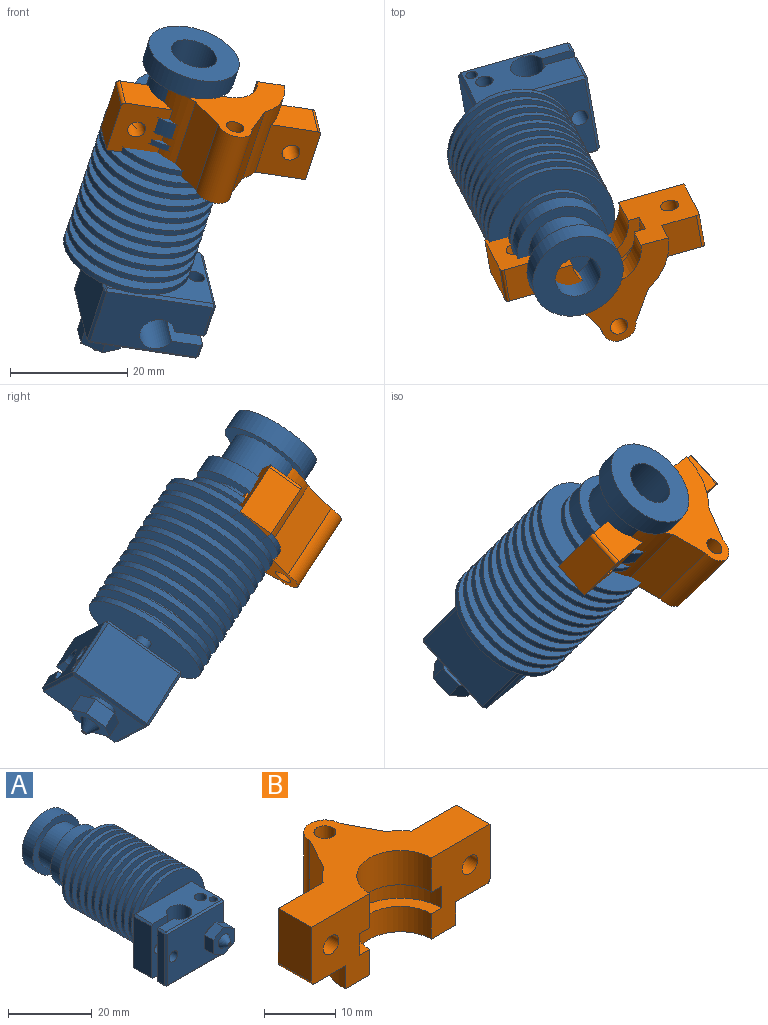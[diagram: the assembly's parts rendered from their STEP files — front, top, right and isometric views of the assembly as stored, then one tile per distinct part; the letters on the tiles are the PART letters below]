
ASSEMBLY  parts=2 mates=1
PART A: 111 faces, bbox 26.7x62.3x22.3 mm
  f0: plane 0.5x0.5mm, normal (-0.58,0.58,-0.58), area 0.2mm2, adj f18,f20,f21
  f1: plane 0.5x0.5mm, normal (0.58,0.58,-0.58), area 0.2mm2, adj f4,f17,f20
  f2: plane 0.5x0.5mm, normal (-0.58,0.58,0.58), area 0.2mm2, adj f6,f18,f19
  f3: plane 0.5x0.5mm, normal (0.58,-0.58,-0.58), area 0.2mm2, adj f4,f9,f16
  f4: plane 10.5x0.5mm, normal (0.71,0,-0.71), area 7.4mm2, adj f1,f3,f27,f51
  f5: plane 0.5x0.5mm, normal (0.58,0.58,0.58), area 0.2mm2, adj f6,f11,f17
  f6: plane 19x0.5mm, normal (0,0.71,0.71), area 13.4mm2, adj f2,f5,f22,f25
  f7: plane 0.5x0.5mm, normal (-0.58,-0.58,-0.58), area 0.2mm2, adj f8,f9,f14
  f8: plane 2.5x0.5mm, normal (-0.71,0,-0.71), area 1.8mm2, adj f7,f50,f51,f52
  f9: plane 19x0.5mm, normal (0,-0.71,-0.71), area 13.4mm2, adj f3,f7,f26,f51
  f10: plane 0.5x0.5mm, normal (0.58,-0.58,0.58), area 0.2mm2, adj f11,f15,f16
  f11: plane 10.5x0.5mm, normal (0.71,0,0.71), area 7.4mm2, adj f5,f10,f22,f27
  f12: plane 0.5x0.5mm, normal (-0.58,-0.58,0.58), area 0.2mm2, adj f13,f14,f15
  f13: plane 2.5x0.5mm, normal (-0.71,0,0.71), area 1.8mm2, adj f12,f22,f50,f52
  f14: plane 15x0.5mm, normal (-0.71,-0.71,0), area 10.6mm2, adj f7,f12,f26,f52
  f15: plane 19x0.5mm, normal (0,-0.71,0.71), area 13.4mm2, adj f10,f12,f22,f26
  f16: plane 15x0.5mm, normal (0.71,-0.71,0), area 10.6mm2, adj f3,f10,f26,f27
  f17: plane 15x0.5mm, normal (0.71,0.71,0), area 10.6mm2, adj f1,f5,f25,f27
  f18: plane 15x0.5mm, normal (-0.71,0.71,0), area 10.6mm2, adj f0,f2,f23,f25
  f19: plane 6x0.5mm, normal (-0.71,0,0.71), area 4.2mm2, adj f2,f22,f23,f24
  f20: plane 19x0.5mm, normal (0,0.71,-0.71), area 13.4mm2, adj f0,f1,f25,f51
  f21: plane 6x0.5mm, normal (-0.71,0,-0.71), area 4.2mm2, adj f0,f23,f24,f51
  f22: plane 19x10.5mm, normal (0,0,1), area 150.5mm2, adj f6,f11,f13,f15,f19,f24,f43,f47
  f23: plane 15x6mm, normal (-1,0,0), area 90mm2, adj f18,f19,f21,f24
  f24: plane 16x5.65mm, normal (0,-1,0), area 83mm2, adj f19,f21,f22,f23,f42,f49,f51
  f25: plane 19x15mm, normal (0,1,0), area 271.8mm2, adj f6,f17,f18,f20,f42,f53
  f26: plane 19x15mm, normal (0,-1,0), area 258.3mm2, adj f9,f14,f15,f16,f40,f41
  f27: plane 15x10.5mm, normal (1,0,0), area 157.5mm2, adj f4,f11,f16,f17
  f28: cylinder r=0.2mm len=3mm, axis (0,1,0), area 3.8mm2, adj f29,f30
  f29: plane 0.4x0.4mm, normal (0,-1,0), area 0.1mm2, adj f28
  f30: plane 1x1mm, normal (0,-1,0), area 0.7mm2, adj f28,f31
  f31: cone r=1.9mm half-angle=35deg, axis (0,1,0), area 18.4mm2, adj f30,f39
  f32: plane 8.08x7mm, normal (0,1,0), area 22.8mm2, adj f33,f34,f35,f36,f37,f38,f40
  f33: plane 3.5x3mm, normal (-0.5,0,0.87), area 12.1mm2, adj f32,f34,f38,f39
  f34: plane 3.5x3mm, normal (0.5,0,0.87), area 12.1mm2, adj f32,f33,f35,f39
  f35: plane 4.04x3mm, normal (1,0,0), area 12.1mm2, adj f32,f34,f36,f39
  f36: plane 3.5x3mm, normal (0.5,0,-0.87), area 12.1mm2, adj f32,f35,f37,f39
  f37: plane 3.5x3mm, normal (-0.5,0,-0.87), area 12.1mm2, adj f32,f36,f38,f39
  f38: plane 4.04x3mm, normal (-1,0,0), area 12.1mm2, adj f32,f33,f37,f39
  f39: plane 8.08x7mm, normal (0,-1,0), area 31.1mm2, adj f31,f33,f34,f35,f36,f37,f38
  f40: cylinder r=2.5mm len=5mm, axis (0,-1,0), area 15.7mm2, adj f26,f32
  f41: cylinder r=1.5mm len=3mm, axis (0,-1,0), area 28.3mm2, adj f26,f50
  f42: cylinder r=1.5mm len=6.5mm, axis (0,-1,0), area 61.3mm2, adj f24,f25
  f43: cylinder r=1mm len=2mm, axis (0,0,-1), area 12.6mm2, adj f22,f44
  f44: plane 2x2mm, normal (0,0,1), area 1.3mm2, adj f43,f45
  f45: cylinder r=0.78mm len=2.45mm, axis (0,0,-1), area 11.9mm2, adj f44,f46
  f46: plane 1.55x1.55mm, normal (0,0,1), area 1.9mm2, adj f45
  f47: cylinder r=1.5mm len=3.45mm, axis (0,0,-1), area 32.5mm2, adj f22,f48
  f48: plane 3x3mm, normal (0,0,1), area 7.1mm2, adj f47
  f49: cylinder r=3.02mm len=16mm, axis (0,0,-1), area 271.5mm2, adj f22,f24,f50,f51
  f50: plane 16x5.65mm, normal (0,1,0), area 83mm2, adj f8,f13,f22,f41,f49,f51,f52
  f51: plane 19x10.5mm, normal (0,0,-1), area 160.7mm2, adj f4,f8,f9,f20,f21,f24,f49,f50
  f52: plane 15x2.5mm, normal (-1,0,0), area 37.5mm2, adj f8,f13,f14,f50
  f53: cylinder r=1.4mm len=2.8mm, axis (0,-1,0), area 18.5mm2, adj f25,f110
  f54: cylinder r=4mm len=8mm, axis (0,-1,0), area 163.4mm2, adj f55,f56
  f55: plane 8x8mm, normal (0,1,0), area 50.3mm2, adj f54
  f56: plane 16x16mm, normal (0,1,0), area 150.8mm2, adj f54,f57
  f57: cylinder r=8mm len=16mm, axis (0,-1,0), area 186mm2, adj f56,f58
  f58: plane 16x16mm, normal (0,-1,0), area 88mm2, adj f57,f59
  f59: cylinder r=6mm len=12mm, axis (0,-1,0), area 226.2mm2, adj f58,f60
  f60: plane 16x16mm, normal (0,1,0), area 88mm2, adj f59,f61
  f61: cylinder r=8mm len=16mm, axis (0,-1,0), area 150.8mm2, adj f60,f62
  f62: plane 16x16mm, normal (0,-1,0), area 137.4mm2, adj f61,f63
  f63: cylinder r=4.5mm len=9mm, axis (0,-1,0), area 42.4mm2, adj f62,f64
  f64: plane 16x16mm, normal (0,1,0), area 137.4mm2, adj f63,f65
  f65: cylinder r=8mm len=16mm, axis (0,-1,0), area 50.3mm2, adj f64,f66
  f66: plane 16x16mm, normal (0,-1,0), area 137.4mm2, adj f65,f67
  f67: cylinder r=4.5mm len=9mm, axis (0,-1,0), area 42.4mm2, adj f66,f68
  f68: plane 22.3x22.3mm, normal (0,1,0), area 327mm2, adj f67,f69
  f69: cylinder r=11.15mm len=22.3mm, axis (0,-1,0), area 70.1mm2, adj f68,f70
  f70: plane 22.3x22.3mm, normal (0,-1,0), area 319.7mm2, adj f69,f71
  f71: cylinder r=4.75mm len=9.5mm, axis (0,-1,0), area 44.8mm2, adj f70,f72
  f72: plane 22.3x22.3mm, normal (0,1,0), area 319.7mm2, adj f71,f73
  f73: cylinder r=11.15mm len=22.3mm, axis (0,-1,0), area 70.1mm2, adj f72,f74
  f74: plane 22.3x22.3mm, normal (0,-1,0), area 312mm2, adj f73,f75
  f75: cylinder r=5mm len=10mm, axis (0,-1,0), area 47.1mm2, adj f74,f76
  f76: plane 22.3x22.3mm, normal (0,1,0), area 312mm2, adj f75,f77
  f77: cylinder r=11.15mm len=22.3mm, axis (0,-1,0), area 70.1mm2, adj f76,f78
  f78: plane 22.3x22.3mm, normal (0,-1,0), area 304mm2, adj f77,f79
  f79: cylinder r=5.25mm len=10.5mm, axis (0,-1,0), area 49.5mm2, adj f78,f80
  f80: plane 22.3x22.3mm, normal (0,1,0), area 304mm2, adj f79,f81
  f81: cylinder r=11.15mm len=22.3mm, axis (0,-1,0), area 70.1mm2, adj f80,f82
  f82: plane 22.3x22.3mm, normal (0,-1,0), area 295.5mm2, adj f81,f83
  f83: cylinder r=5.5mm len=11mm, axis (0,-1,0), area 51.8mm2, adj f82,f84
  f84: plane 22.3x22.3mm, normal (0,1,0), area 295.5mm2, adj f83,f85
  f85: cylinder r=11.15mm len=22.3mm, axis (0,-1,0), area 70.1mm2, adj f84,f86
  f86: plane 22.3x22.3mm, normal (0,-1,0), area 286.7mm2, adj f85,f87
  f87: cylinder r=5.75mm len=11.5mm, axis (0,-1,0), area 54.2mm2, adj f86,f88
  f88: plane 22.3x22.3mm, normal (0,1,0), area 286.7mm2, adj f87,f89
  f89: cylinder r=11.15mm len=22.3mm, axis (0,-1,0), area 70.1mm2, adj f88,f90
  f90: plane 22.3x22.3mm, normal (0,-1,0), area 277.5mm2, adj f89,f91
  f91: cylinder r=6mm len=12mm, axis (0,-1,0), area 56.5mm2, adj f90,f92
  f92: plane 22.3x22.3mm, normal (0,1,0), area 277.5mm2, adj f91,f93
  f93: cylinder r=11.15mm len=22.3mm, axis (0,-1,0), area 70.1mm2, adj f92,f94
  f94: plane 22.3x22.3mm, normal (0,-1,0), area 267.9mm2, adj f93,f95
  f95: cylinder r=6.25mm len=12.5mm, axis (0,-1,0), area 58.9mm2, adj f94,f96
  f96: plane 22.3x22.3mm, normal (0,1,0), area 267.9mm2, adj f95,f97
  f97: cylinder r=11.15mm len=22.3mm, axis (0,-1,0), area 70.1mm2, adj f96,f98
  f98: plane 22.3x22.3mm, normal (0,-1,0), area 257.8mm2, adj f97,f99
  f99: cylinder r=6.5mm len=13mm, axis (0,-1,0), area 61.3mm2, adj f98,f100
  f100: plane 22.3x22.3mm, normal (0,1,0), area 257.8mm2, adj f99,f101
  f101: cylinder r=11.15mm len=22.3mm, axis (0,-1,0), area 70.1mm2, adj f100,f102
  f102: plane 22.3x22.3mm, normal (0,-1,0), area 247.4mm2, adj f101,f103
  f103: cylinder r=6.75mm len=13.5mm, axis (0,-1,0), area 63.6mm2, adj f102,f104
  f104: plane 22.3x22.3mm, normal (0,1,0), area 247.4mm2, adj f103,f105
  f105: cylinder r=11.15mm len=22.3mm, axis (0,-1,0), area 70.1mm2, adj f104,f106
  f106: plane 22.3x22.3mm, normal (0,-1,0), area 236.6mm2, adj f105,f107
  f107: cylinder r=7mm len=14mm, axis (0,-1,0), area 66mm2, adj f106,f108
  f108: plane 22.3x22.3mm, normal (0,1,0), area 236.6mm2, adj f107,f109
  f109: cylinder r=11.15mm len=22.3mm, axis (0,-1,0), area 70.1mm2, adj f108,f110
  f110: plane 22.3x22.3mm, normal (0,-1,0), area 384.4mm2, adj f53,f109
PART B: 25 faces, bbox 35.6x18x14 mm
  f0: cylinder r=11mm len=14mm, axis (0,0,-1), area 80.4mm2, adj f3,f4,f10,f13,f18,f20
  f1: cylinder r=11mm len=14mm, axis (0,0,-1), area 80.4mm2, adj f3,f4,f9,f14,f16,f17
  f2: cylinder r=6.15mm len=12.3mm, axis (0,0,1), area 114mm2, adj f3,f6,f13,f14
  f3: plane 35.61x18mm, normal (0,0,1), area 273.8mm2, adj f0,f1,f2,f9,f10,f11,f12,f13
  f4: plane 22x18mm, normal (0,0,-1), area 175.4mm2, adj f0,f1,f5,f9,f10,f11,f12,f13
  f5: cylinder r=6.15mm len=12.3mm, axis (0,0,1), area 84.6mm2, adj f4,f7,f13,f14
  f6: plane 16.3x8.15mm, normal (0,0,-1), area 44.9mm2, adj f2,f8,f13,f14
  f7: plane 16.3x8.15mm, normal (0,0,1), area 44.9mm2, adj f5,f8,f13,f14
  f8: cylinder r=8.15mm len=16.3mm, axis (0,0,-1), area 95.2mm2, adj f6,f7,f13,f14
  f9: plane 14x5.9mm, normal (-0.88,0.47,0), area 93.5mm2, adj f1,f3,f4,f11
  f10: plane 14x5.9mm, normal (0.88,0.47,0), area 93.5mm2, adj f0,f3,f4,f11
  f11: cylinder r=3mm len=14mm, axis (0,0,-1), area 131.3mm2, adj f3,f4,f9,f10
  f12: cylinder r=1.55mm len=14mm, axis (0,0,1), area 136.3mm2, adj f3,f4
  f13: plane 14x11.65mm, normal (0,-1,0), area 120.9mm2, adj f0,f2,f3,f4,f5,f6,f7,f8
  f14: plane 14x11.65mm, normal (0,-1,0), area 120.9mm2, adj f1,f2,f3,f4,f5,f6,f7,f8
  f15: plane 9.4x6.57mm, normal (-1,0,0), area 61.7mm2, adj f3,f14,f16,f22
  f16: plane 10x8.98mm, normal (0,1,0), area 82.2mm2, adj f1,f3,f15,f17,f22,f24
  f17: plane 8.38x6.57mm, normal (0,0,-1), area 45.3mm2, adj f1,f14,f16,f22
  f18: plane 10x8.98mm, normal (0,1,0), area 82.2mm2, adj f0,f3,f19,f20,f21,f23
  f19: plane 9.4x6.57mm, normal (1,0,0), area 61.7mm2, adj f3,f13,f18,f21
  f20: plane 8.38x6.57mm, normal (0,0,-1), area 45.3mm2, adj f0,f13,f18,f21
  f21: cylinder r=0.6mm len=6.57mm, axis (0,1,0), area 6.2mm2, adj f13,f18,f19,f20
  f22: cylinder r=0.6mm len=6.57mm, axis (0,-1,0), area 6.2mm2, adj f14,f15,f16,f17
  f23: cylinder r=1.55mm len=6.57mm, axis (0,-1,0), area 63.9mm2, adj f13,f18
  f24: cylinder r=1.55mm len=6.57mm, axis (0,-1,0), area 63.9mm2, adj f14,f16
PLACE A rot(axis=(0,-0.47,-0.88),162.3deg) t=(-21.38,11.41,-10.28)mm
PLACE B rot(axis=(-0.99,-0.11,0.11),146.1deg) t=(-10.77,3.78,3.08)mm
MATE slider B.f4 <-> A.f53  axis (0.27,-0.53,0.81) through (-16.63,2.12,3.96)mm
